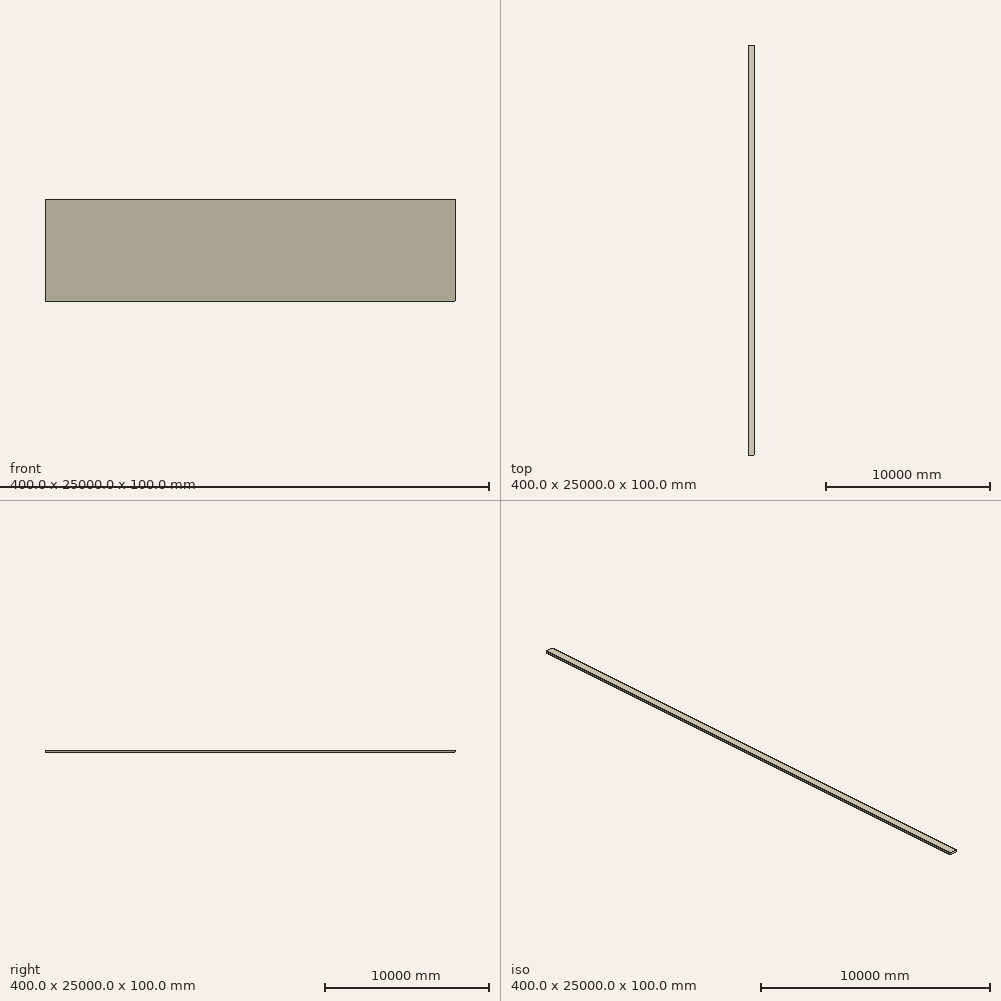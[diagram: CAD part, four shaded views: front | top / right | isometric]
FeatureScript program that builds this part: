
annotation { "Feature Type Name" : "Feature", "Feature Type Description" : "" }
export const myFeature = defineFeature(function(context is Context, id is Id, definition is map)
    precondition{}
    {
        {
            var Q0;
            Q0=qCreatedBy(makeId("Front.planeOp"),FACE);
            var sketch = newSketch(context, id + "F0", { "sketchPlane" : qUnion([Q0])});
            skLineSegment(sketch, "E0.bottom", {"start": v(0, 0) * mm, "end": v(400, 0) * mm});
            skLineSegment(sketch, "E0.top", {"start": v(0, 100) * mm, "end": v(400, 100) * mm});
            skLineSegment(sketch, "E0.left", {"start": v(0, 0) * mm, "end": v(0, 100) * mm});
            skLineSegment(sketch, "E0.right", {"start": v(400, 0) * mm, "end": v(400, 100) * mm});
            skSolve(sketch);
        }
        {
            var Q0;
            Q0=qSketchRegion(id+"F0",true);
            extrude(context, id + "F1", {"entities" : qUnion([Q0]), "depth" : 25000 * mm, "offsetDistance" : 25 * mm});
        }
    });
